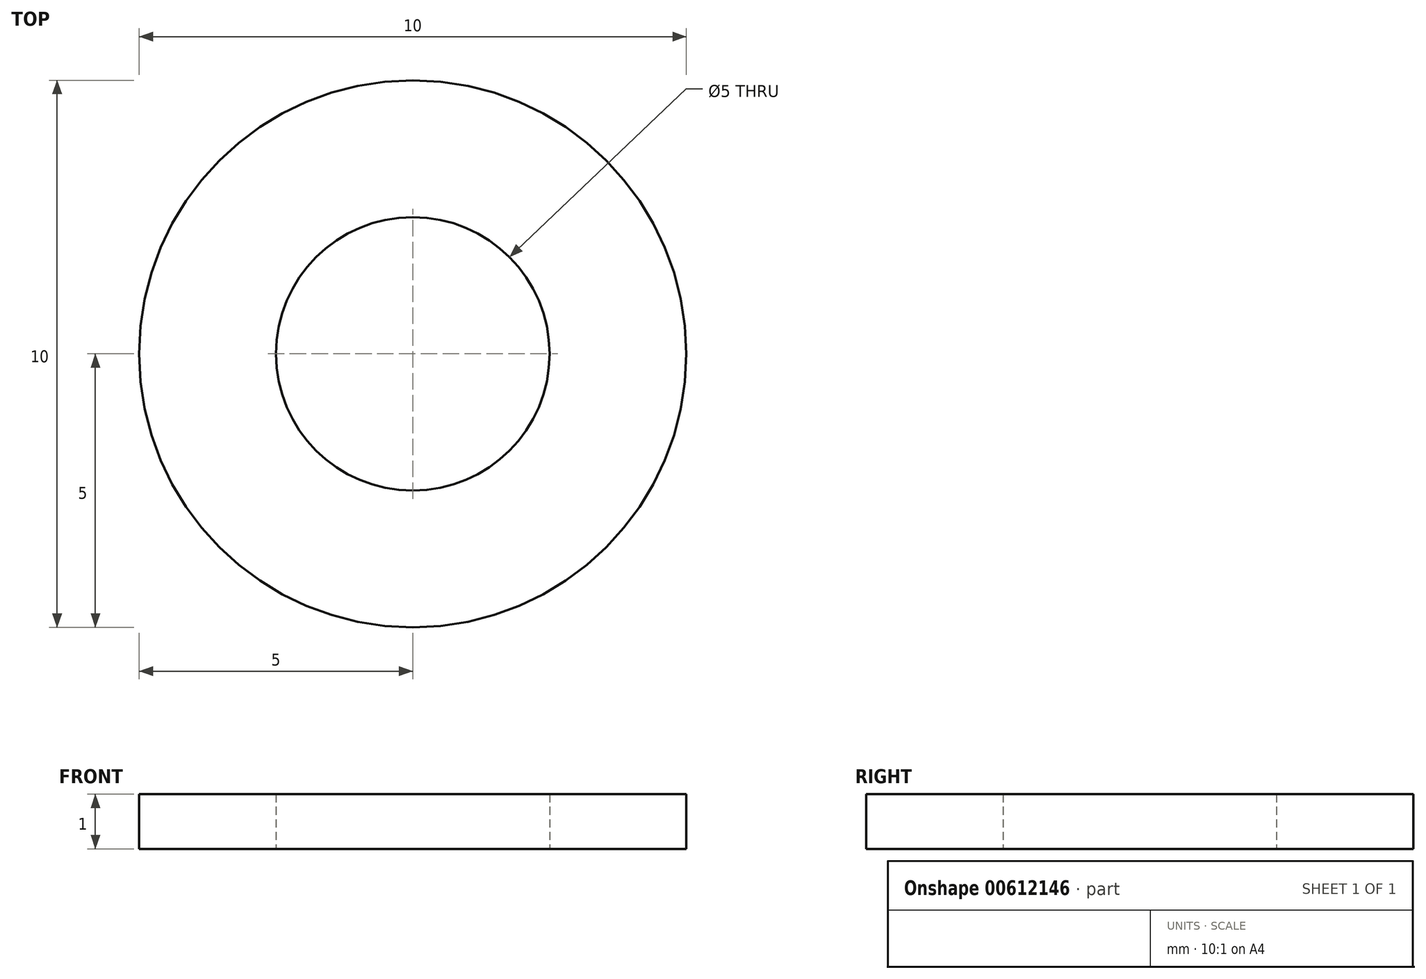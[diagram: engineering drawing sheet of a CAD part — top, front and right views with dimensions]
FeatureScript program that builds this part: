
annotation { "Feature Type Name" : "Feature", "Feature Type Description" : "" }
export const myFeature = defineFeature(function(context is Context, id is Id, definition is map)
    precondition{}
    {
        {
            var Q0;
            Q0=qCreatedBy(makeId("Top.planeOp"),FACE);
            var sketch = newSketch(context, id + "F0", { "sketchPlane" : qUnion([Q0])});
            skCircle(sketch, "E0", {"center": v(0, 0) * mm, "radius": 5 * mm});
            skCircle(sketch, "E1", {"center": v(0, 0) * mm, "radius": 2.5 * mm});
            skSolve(sketch);
        }
        {
            var Q0;
            Q0=makeQuery(id+"F0.imprint","IMPRINT",FACE,{"disambiguationData":[TD([[makeQuery(id+"F0.imprint","IMPRINT",EDGE,{"derivedFrom":sQuery(id+"F0.wireOp",EDGE,"E0")}),1.0]])]});
            var Q1;
            Q1=sQuery(id+"F0.wireOp",EDGE,"E0");
            extrude(context, id + "F1", {"entities" : qUnion([Q0]), "surfaceEntities" : qUnion([Q1]), "depth" : 1 * mm, "offsetDistance" : 25 * mm});
        }
    });
